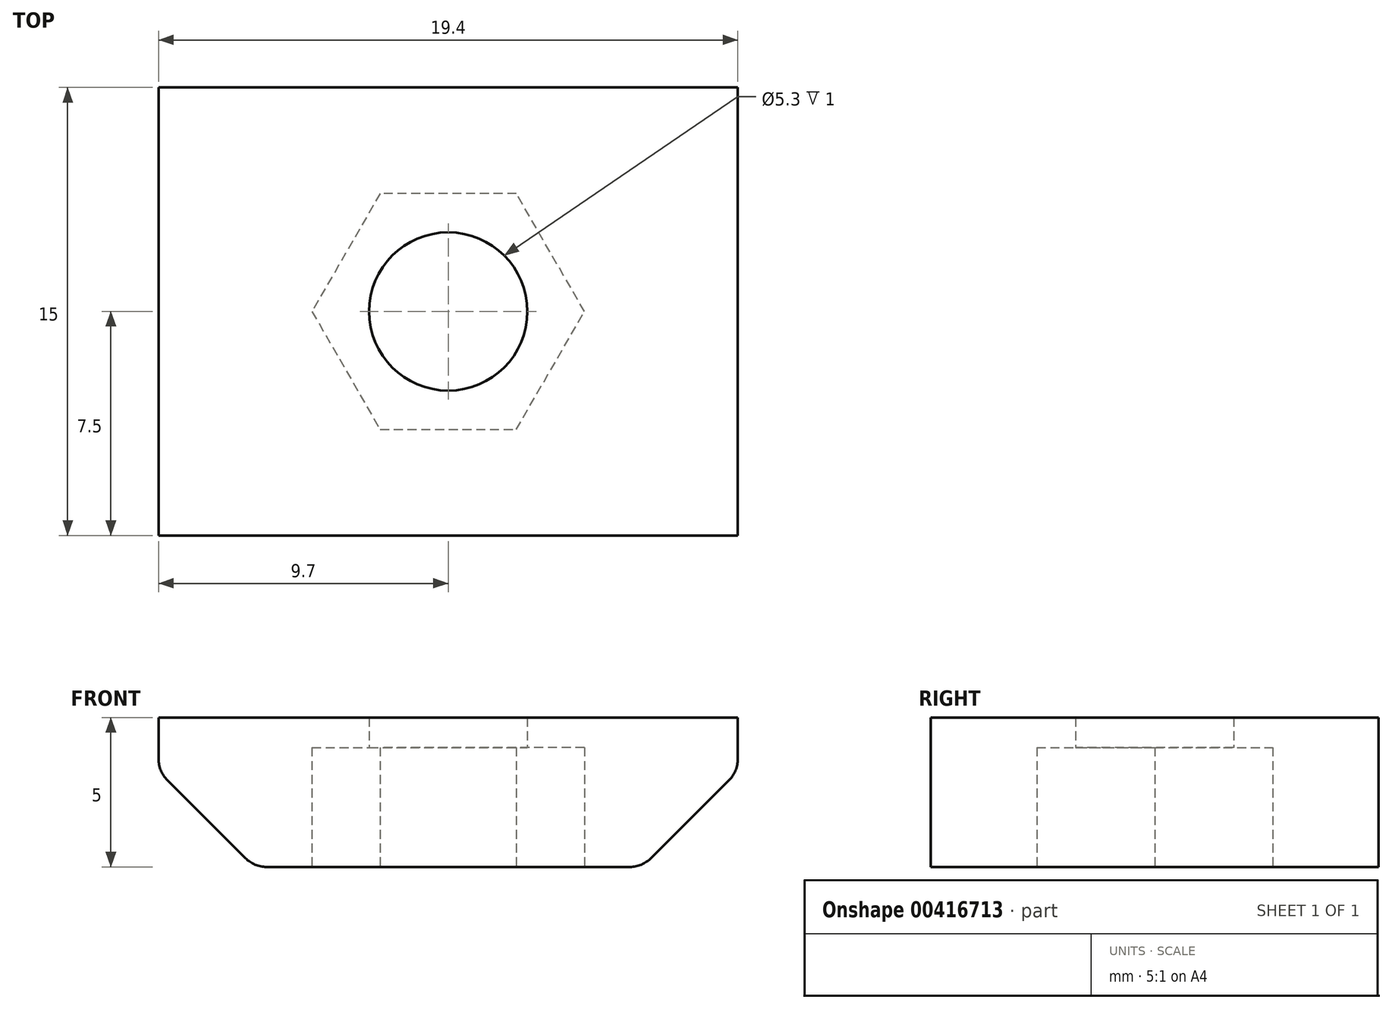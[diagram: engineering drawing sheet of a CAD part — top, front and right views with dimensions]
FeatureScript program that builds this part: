
annotation { "Feature Type Name" : "Feature", "Feature Type Description" : "" }
export const myFeature = defineFeature(function(context is Context, id is Id, definition is map)
    precondition{}
    {
        {
            var Q0;
            Q0=qCreatedBy(makeId("Front.planeOp"),FACE);
            var sketch = newSketch(context, id + "F0", { "sketchPlane" : qUnion([Q0])});
            skLineSegment(sketch, "E0.bottom", {"start": v(9.7, -2.5) * mm, "end": v(-9.7, -2.5) * mm});
            skLineSegment(sketch, "E0.top", {"start": v(9.7, 2.5) * mm, "end": v(-9.7, 2.5) * mm});
            skLineSegment(sketch, "E0.left", {"start": v(9.7, -2.5) * mm, "end": v(9.7, 2.5) * mm});
            skLineSegment(sketch, "E0.right", {"start": v(-9.7, -2.5) * mm, "end": v(-9.7, 2.5) * mm});
            skPoint(sketch, "E0.middle", {"position": v(0, 0) * mm});
            skLineSegment(sketch, "E1.bottom", {"start": v(-4.88, 2.5) * mm, "end": v(4.88, 2.5) * mm});
            skLineSegment(sketch, "E1.top", {"start": v(-4.88, 7.5) * mm, "end": v(4.88, 7.5) * mm});
            skLineSegment(sketch, "E1.left", {"start": v(-4.88, 2.5) * mm, "end": v(-4.88, 7.5) * mm});
            skLineSegment(sketch, "E1.right", {"start": v(4.88, 2.5) * mm, "end": v(4.88, 7.5) * mm});
            skSolve(sketch);
        }
        {
            var Q0;
            Q0=makeQuery(id+"F0.imprint","IMPRINT",FACE,{"disambiguationData":[TD([[makeQuery(id+"F0.imprint","IMPRINT",EDGE,{"derivedFrom":sQuery(id+"F0.wireOp",EDGE,"E0.bottom")}),-1.0]])]});
            var Q1;
            Q1=makeQuery(id+"F0.imprint","IMPRINT",FACE,{"disambiguationData":[TD([[makeQuery(id+"F0.imprint","IMPRINT",EDGE,{"derivedFrom":sQuery(id+"F0.wireOp",EDGE,"E1.bottom")}),1.0]])]});
            extrude(context, id + "F1", {"entities" : qUnion([Q0, Q1]), "depth" : 15 * mm});
        }
        {
            var Q0;
            Q0=makeQuery(id+"F1.opExtrude","SWEPT_EDGE",EDGE,{"disambiguationData":[OSD([sQuery(id+"F0.wireOp",EDGE,"E0.bottom"),sQuery(id+"F0.wireOp",EDGE,"E0.left")])]});
            var Q1;
            Q1=makeQuery(id+"F1.opExtrude","SWEPT_EDGE",EDGE,{"disambiguationData":[OSD([sQuery(id+"F0.wireOp",EDGE,"E0.bottom"),sQuery(id+"F0.wireOp",EDGE,"E0.right")])]});
            chamfer(context, id + "F2", {"entities" : qUnion([Q0, Q1]), "width" : 3.2 * mm, "tangentPropagation" : true});
        }
        {
            var Q0;
            Q0=makeQuery(id+"F1.opExtrude","SWEPT_FACE",FACE,{"disambiguationData":[OSD([sQuery(id+"F0.wireOp",EDGE,"E0.bottom")])]});
            var sketch = newSketch(context, id + "F3", { "sketchPlane" : qUnion([Q0])});
            skPoint(sketch, "E2", {"position": v(0, 7.5) * mm});
            skPoint(sketch, "E2.positionSnap0", {"position": v(6.5, 7.5) * mm});
            skPoint(sketch, "E2.positionSnap1", {"position": v(0, 15) * mm});
            skCircle(sketch, "E3.cCircle", {"center": v(0, 7.5) * mm, "radius": 3.95 * mm, "construction": true});
            skLineSegment(sketch, "E3.0", {"start": v(2.28, 3.55) * mm, "end": v(-2.28, 3.55) * mm});
            skLineSegment(sketch, "E3.1", {"start": v(-2.28, 3.55) * mm, "end": v(-4.56, 7.5) * mm});
            skLineSegment(sketch, "E3.2", {"start": v(-4.56, 7.5) * mm, "end": v(-2.28, 11.45) * mm});
            skLineSegment(sketch, "E3.3", {"start": v(-2.28, 11.45) * mm, "end": v(2.28, 11.45) * mm});
            skLineSegment(sketch, "E3.4", {"start": v(2.28, 11.45) * mm, "end": v(4.56, 7.5) * mm});
            skLineSegment(sketch, "E3.5", {"start": v(4.56, 7.5) * mm, "end": v(2.28, 3.55) * mm});
            skPoint(sketch, "E3.0.midPoint", {"position": v(0, 3.55) * mm});
            skCircle(sketch, "E4", {"center": v(0, 7.5) * mm, "radius": 2.65 * mm});
            skSolve(sketch);
        }
        {
            var Q0;
            Q0=makeQuery(id+"F3.imprint","IMPRINT",FACE,{"disambiguationData":[TD([[makeQuery(id+"F3.imprint","IMPRINT",EDGE,{"derivedFrom":sQuery(id+"F3.wireOp",EDGE,"E4")}),1.0]])]});
            extrude(context, id + "F4", {"entities" : qUnion([Q0]), "operationType" : NewBodyOperationType.REMOVE, "endBound" : BoundingType.THROUGH_ALL, "oppositeDirection" : true, "depth" : 25 * mm});
        }
        {
            var Q0;
            Q0=makeQuery(id+"F3.imprint","IMPRINT",FACE,{"disambiguationData":[TD([[makeQuery(id+"F3.imprint","IMPRINT",EDGE,{"derivedFrom":sQuery(id+"F3.wireOp",EDGE,"E3.0")}),-1.0]])]});
            extrude(context, id + "F5", {"entities" : qUnion([Q0]), "operationType" : NewBodyOperationType.REMOVE, "oppositeDirection" : true, "depth" : 4 * mm});
        }
        {
            var Q0;
            {var subQ0=sQuery(id+"F0.wireOp",EDGE,"E0.bottom");Q0=makeQuery(id+"F2.opChamfer","BLEND_EDGE",EDGE,{"blendedFrom":[makeQuery(id+"F1.opExtrude","SWEPT_EDGE",EDGE,{"disambiguationData":[OSD([subQ0,sQuery(id+"F0.wireOp",EDGE,"E0.right")])]}),makeQuery(id+"F1.opExtrude","SWEPT_FACE",FACE,{"disambiguationData":[OSD([subQ0])]})],"blendedInto":[makeQuery(id+"F1.opExtrude","SWEPT_FACE",FACE,{"disambiguationData":[OSD([subQ0])]})]});}
            var Q1;
            {var subQ0=sQuery(id+"F0.wireOp",EDGE,"E0.bottom");Q1=makeQuery(id+"F2.opChamfer","BLEND_EDGE",EDGE,{"blendedFrom":[makeQuery(id+"F1.opExtrude","SWEPT_EDGE",EDGE,{"disambiguationData":[OSD([subQ0,sQuery(id+"F0.wireOp",EDGE,"E0.left")])]}),makeQuery(id+"F1.opExtrude","SWEPT_FACE",FACE,{"disambiguationData":[OSD([subQ0])]})],"blendedInto":[makeQuery(id+"F1.opExtrude","SWEPT_FACE",FACE,{"disambiguationData":[OSD([subQ0])]})]});}
            var Q2;
            {var subQ0=sQuery(id+"F0.wireOp",EDGE,"E0.left");Q2=makeQuery(id+"F2.opChamfer","BLEND_EDGE",EDGE,{"blendedFrom":[makeQuery(id+"F1.opExtrude","SWEPT_EDGE",EDGE,{"disambiguationData":[OSD([sQuery(id+"F0.wireOp",EDGE,"E0.bottom"),subQ0])]}),makeQuery(id+"F1.opExtrude","SWEPT_FACE",FACE,{"disambiguationData":[OSD([subQ0])]})],"blendedInto":[makeQuery(id+"F1.opExtrude","SWEPT_FACE",FACE,{"disambiguationData":[OSD([subQ0])]})]});}
            var Q3;
            {var subQ0=sQuery(id+"F0.wireOp",EDGE,"E0.right");Q3=makeQuery(id+"F2.opChamfer","BLEND_EDGE",EDGE,{"blendedFrom":[makeQuery(id+"F1.opExtrude","SWEPT_EDGE",EDGE,{"disambiguationData":[OSD([sQuery(id+"F0.wireOp",EDGE,"E0.bottom"),subQ0])]}),makeQuery(id+"F1.opExtrude","SWEPT_FACE",FACE,{"disambiguationData":[OSD([subQ0])]})],"blendedInto":[makeQuery(id+"F1.opExtrude","SWEPT_FACE",FACE,{"disambiguationData":[OSD([subQ0])]})]});}
            fillet(context, id + "F6", {"entities" : qUnion([Q0, Q1, Q2, Q3]), "radius" : 1 * mm, "tangentPropagation" : true, "allowEdgeOverflow" : false});
        }
    });
